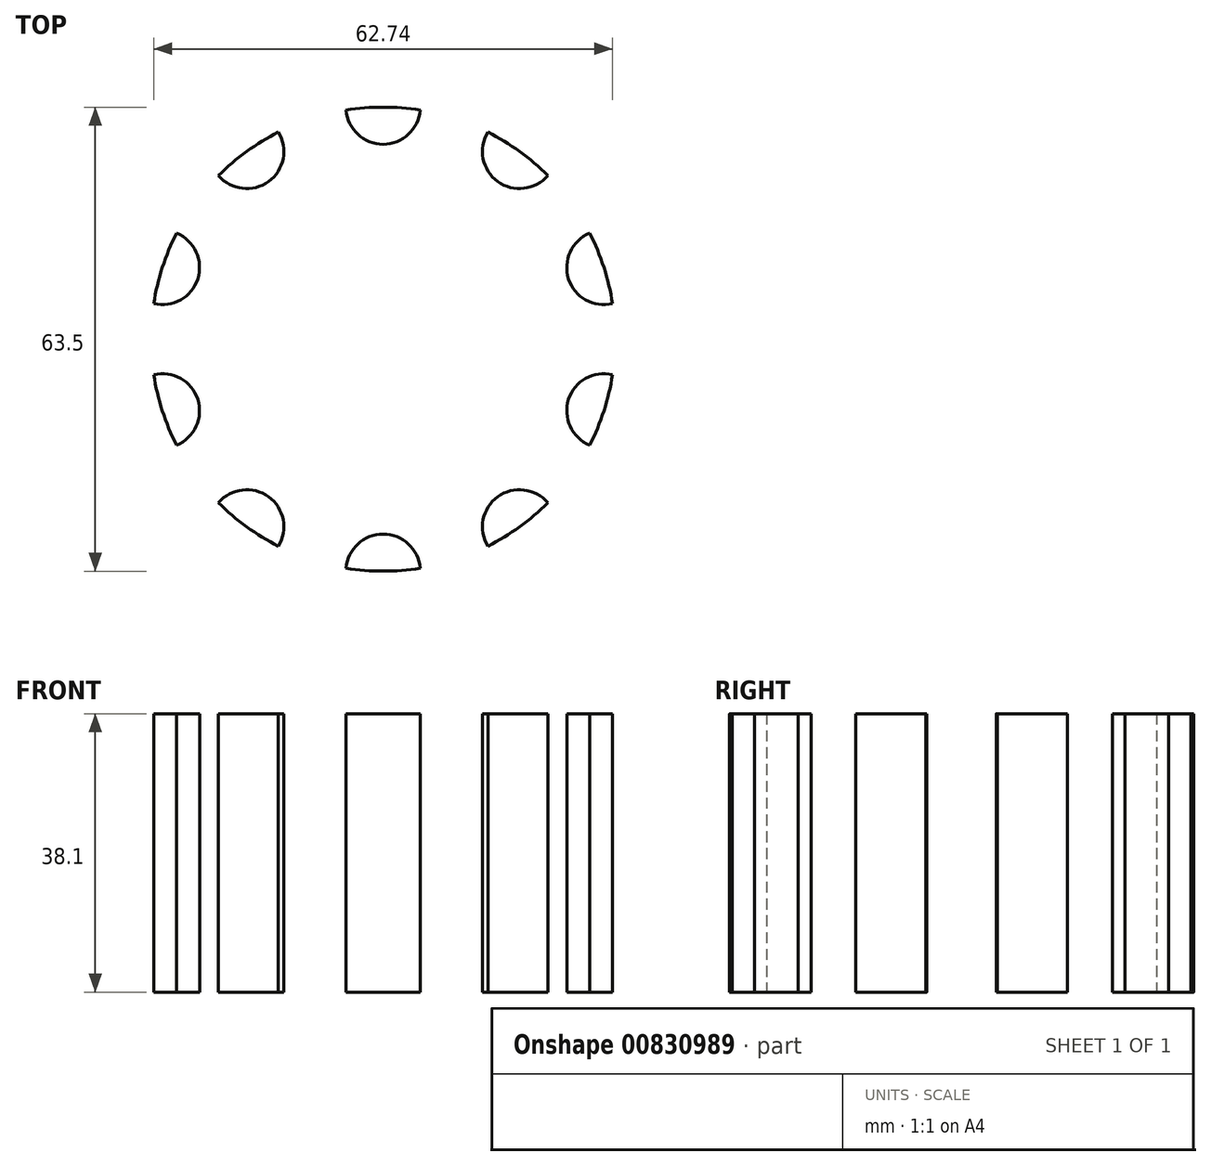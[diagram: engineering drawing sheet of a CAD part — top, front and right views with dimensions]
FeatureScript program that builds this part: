
annotation { "Feature Type Name" : "Feature", "Feature Type Description" : "" }
export const myFeature = defineFeature(function(context is Context, id is Id, definition is map)
    precondition{}
    {
        {
            var Q0;
            Q0=qCreatedBy(makeId("Top.planeOp"),FACE);
            var sketch = newSketch(context, id + "F0", { "sketchPlane" : qUnion([Q0])});
            skCircle(sketch, "E0", {"center": v(0, 0) * mm, "radius": 31.75 * mm});
            skSolve(sketch);
        }
        {
            var Q0;
            Q0=qSketchRegion(id+"F0",true);
            extrude(context, id + "F1", {"entities" : qUnion([Q0]), "depth" : 38.1 * mm});
        }
        {
            var Q0;
            Q0=qCreatedBy(makeId("Top.planeOp"),FACE);
            var sketch = newSketch(context, id + "F2", { "sketchPlane" : qUnion([Q0])});
            skCircle(sketch, "E1", {"center": v(0, 31.75) * mm, "radius": 5.08 * mm});
            skCircle(sketch, "E2.1.0", {"center": v(-18.66, 25.69) * mm, "radius": 5.08 * mm});
            skCircle(sketch, "E2.2.0", {"center": v(-30.2, 9.81) * mm, "radius": 5.08 * mm});
            skCircle(sketch, "E2.3.0", {"center": v(-30.2, -9.81) * mm, "radius": 5.08 * mm});
            skCircle(sketch, "E2.4.0", {"center": v(-18.66, -25.69) * mm, "radius": 5.08 * mm});
            skCircle(sketch, "E2.5.0", {"center": v(0, -31.75) * mm, "radius": 5.08 * mm});
            skCircle(sketch, "E2.6.0", {"center": v(18.66, -25.69) * mm, "radius": 5.08 * mm});
            skCircle(sketch, "E2.7.0", {"center": v(30.2, -9.81) * mm, "radius": 5.08 * mm});
            skCircle(sketch, "E2.8.0", {"center": v(30.2, 9.81) * mm, "radius": 5.08 * mm});
            skCircle(sketch, "E2.9.0", {"center": v(18.66, 25.69) * mm, "radius": 5.08 * mm});
            skPoint(sketch, "E2.center", {"position": v(0, 0) * mm});
            skSolve(sketch);
        }
        {
            var Q0;
            Q0=qSketchRegion(id+"F2",true);
            extrude(context, id + "F3", {"entities" : qUnion([Q0]), "depth" : 50.8 * mm});
        }
        {
            var Q0;
            Q0=makeQuery(id+"F3.opExtrude","SWEPT_BODY",BODY,{"disambiguationData":[OSD([sQuery(id+"F2.wireOp",EDGE,"E2.5.0")])]});
            var Q1;
            Q1=makeQuery(id+"F1.opExtrude","SWEPT_BODY",BODY,{"disambiguationData":[OSD([sQuery(id+"F0.wireOp",EDGE,"E0")])]});
            booleanBodies(context, id + "F4", {"operationType" : BooleanOperationType.INTERSECTION, "tools" : qUnion([Q0, Q1]), "keepTools" : true});
        }
        {
            var Q0;
            Q0=makeQuery(id+"F1.opExtrude","SWEPT_BODY",BODY,{"disambiguationData":[OSD([sQuery(id+"F0.wireOp",EDGE,"E0")])]});
            var Q1;
            Q1=makeQuery(id+"F3.opExtrude","SWEPT_BODY",BODY,{"disambiguationData":[OSD([sQuery(id+"F2.wireOp",EDGE,"E2.6.0")])]});
            booleanBodies(context, id + "F5", {"operationType" : BooleanOperationType.INTERSECTION, "tools" : qUnion([Q0, Q1]), "keepTools" : true});
        }
        {
            var Q0;
            Q0=makeQuery(id+"F3.opExtrude","SWEPT_BODY",BODY,{"disambiguationData":[OSD([sQuery(id+"F2.wireOp",EDGE,"E2.7.0")])]});
            var Q1;
            Q1=makeQuery(id+"F1.opExtrude","SWEPT_BODY",BODY,{"disambiguationData":[OSD([sQuery(id+"F0.wireOp",EDGE,"E0")])]});
            booleanBodies(context, id + "F6", {"operationType" : BooleanOperationType.INTERSECTION, "tools" : qUnion([Q0, Q1]), "keepTools" : true});
        }
        {
            var Q0;
            Q0=makeQuery(id+"F1.opExtrude","SWEPT_BODY",BODY,{"disambiguationData":[OSD([sQuery(id+"F0.wireOp",EDGE,"E0")])]});
            var Q1;
            Q1=makeQuery(id+"F3.opExtrude","SWEPT_BODY",BODY,{"disambiguationData":[OSD([sQuery(id+"F2.wireOp",EDGE,"E2.8.0")])]});
            booleanBodies(context, id + "F7", {"operationType" : BooleanOperationType.INTERSECTION, "tools" : qUnion([Q0, Q1]), "keepTools" : true});
        }
        {
            var Q0;
            Q0=makeQuery(id+"F1.opExtrude","SWEPT_BODY",BODY,{"disambiguationData":[OSD([sQuery(id+"F0.wireOp",EDGE,"E0")])]});
            var Q1;
            Q1=makeQuery(id+"F3.opExtrude","SWEPT_BODY",BODY,{"disambiguationData":[OSD([sQuery(id+"F2.wireOp",EDGE,"E2.9.0")])]});
            booleanBodies(context, id + "F8", {"operationType" : BooleanOperationType.INTERSECTION, "tools" : qUnion([Q0, Q1]), "keepTools" : true});
        }
        {
            var Q0;
            Q0=makeQuery(id+"F3.opExtrude","SWEPT_BODY",BODY,{"disambiguationData":[OSD([sQuery(id+"F2.wireOp",EDGE,"E1")])]});
            var Q1;
            Q1=makeQuery(id+"F1.opExtrude","SWEPT_BODY",BODY,{"disambiguationData":[OSD([sQuery(id+"F0.wireOp",EDGE,"E0")])]});
            booleanBodies(context, id + "F9", {"operationType" : BooleanOperationType.INTERSECTION, "tools" : qUnion([Q0, Q1]), "keepTools" : true});
        }
        {
            var Q0;
            Q0=makeQuery(id+"F3.opExtrude","SWEPT_BODY",BODY,{"disambiguationData":[OSD([sQuery(id+"F2.wireOp",EDGE,"E2.1.0")])]});
            var Q1;
            Q1=makeQuery(id+"F1.opExtrude","SWEPT_BODY",BODY,{"disambiguationData":[OSD([sQuery(id+"F0.wireOp",EDGE,"E0")])]});
            booleanBodies(context, id + "F10", {"operationType" : BooleanOperationType.INTERSECTION, "tools" : qUnion([Q0, Q1]), "keepTools" : true});
        }
        {
            var Q0;
            Q0=makeQuery(id+"F1.opExtrude","SWEPT_BODY",BODY,{"disambiguationData":[OSD([sQuery(id+"F0.wireOp",EDGE,"E0")])]});
            var Q1;
            Q1=makeQuery(id+"F3.opExtrude","SWEPT_BODY",BODY,{"disambiguationData":[OSD([sQuery(id+"F2.wireOp",EDGE,"E2.2.0")])]});
            booleanBodies(context, id + "F11", {"operationType" : BooleanOperationType.INTERSECTION, "tools" : qUnion([Q0, Q1]), "keepTools" : true});
        }
        {
            var Q0;
            Q0=makeQuery(id+"F1.opExtrude","SWEPT_BODY",BODY,{"disambiguationData":[OSD([sQuery(id+"F0.wireOp",EDGE,"E0")])]});
            var Q1;
            Q1=makeQuery(id+"F3.opExtrude","SWEPT_BODY",BODY,{"disambiguationData":[OSD([sQuery(id+"F2.wireOp",EDGE,"E2.3.0")])]});
            booleanBodies(context, id + "F12", {"operationType" : BooleanOperationType.INTERSECTION, "tools" : qUnion([Q0, Q1]), "keepTools" : true});
        }
        {
            var Q0;
            Q0=makeQuery(id+"F1.opExtrude","SWEPT_BODY",BODY,{"disambiguationData":[OSD([sQuery(id+"F0.wireOp",EDGE,"E0")])]});
            var Q1;
            Q1=makeQuery(id+"F3.opExtrude","SWEPT_BODY",BODY,{"disambiguationData":[OSD([sQuery(id+"F2.wireOp",EDGE,"E2.4.0")])]});
            booleanBodies(context, id + "F13", {"operationType" : BooleanOperationType.INTERSECTION, "tools" : qUnion([Q0, Q1])});
        }
        {
            var Q0;
            Q0=makeQuery(id+"F3.opExtrude","SWEPT_BODY",BODY,{"disambiguationData":[OSD([sQuery(id+"F2.wireOp",EDGE,"E2.9.0")])]});
            var Q1;
            Q1=makeQuery(id+"F3.opExtrude","SWEPT_BODY",BODY,{"disambiguationData":[OSD([sQuery(id+"F2.wireOp",EDGE,"E2.8.0")])]});
            var Q2;
            Q2=makeQuery(id+"F3.opExtrude","SWEPT_BODY",BODY,{"disambiguationData":[OSD([sQuery(id+"F2.wireOp",EDGE,"E2.7.0")])]});
            var Q3;
            Q3=makeQuery(id+"F3.opExtrude","SWEPT_BODY",BODY,{"disambiguationData":[OSD([sQuery(id+"F2.wireOp",EDGE,"E2.6.0")])]});
            var Q4;
            Q4=makeQuery(id+"F3.opExtrude","SWEPT_BODY",BODY,{"disambiguationData":[OSD([sQuery(id+"F2.wireOp",EDGE,"E2.5.0")])]});
            var Q5;
            Q5=makeQuery(id+"F3.opExtrude","SWEPT_BODY",BODY,{"disambiguationData":[OSD([sQuery(id+"F2.wireOp",EDGE,"E2.3.0")])]});
            var Q6;
            Q6=makeQuery(id+"F3.opExtrude","SWEPT_BODY",BODY,{"disambiguationData":[OSD([sQuery(id+"F2.wireOp",EDGE,"E2.1.0")])]});
            var Q7;
            Q7=makeQuery(id+"F3.opExtrude","SWEPT_BODY",BODY,{"disambiguationData":[OSD([sQuery(id+"F2.wireOp",EDGE,"E2.2.0")])]});
            var Q8;
            Q8=makeQuery(id+"F3.opExtrude","SWEPT_BODY",BODY,{"disambiguationData":[OSD([sQuery(id+"F2.wireOp",EDGE,"E1")])]});
            deleteBodies(context, id + "F14", {"entities" : qUnion([Q0, Q1, Q2, Q3, Q4, Q5, Q6, Q7, Q8])});
        }
    });
